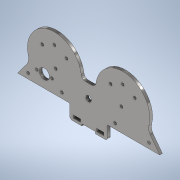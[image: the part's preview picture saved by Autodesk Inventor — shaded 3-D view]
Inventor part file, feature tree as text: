
AUTODESK INVENTOR PART (.ipt)
format: ipt  version: 2022 (Build 260153000, 153)  size: 521,216 bytes
history: native  units: mm
features: other x31, reference x18, sketch x7, chamfer x4, mirror x3, projected_geometry x3
ambient origin geometry x8: Origin, YZ Plane, XZ Plane, XY Plane, X Axis, Y Axis, Z Axis, Center Point
bodies: Body1 (feature_tree)
feature tree (66):
  other  "Твердое тело1"
  other  "Грань1"
  other  "Грань2"
  mirror  "Зеркальное отражение1"
  other  "УглСкругление1"
  other  "УглСкругление2"
  chamfer  "Фаска1"  Distance=1.0mm
  mirror  "Зеркальное отражение2"
  mirror  "Зеркальное отражение3"
  chamfer  "Фаска2"  Distance=3.0mm
  chamfer  "Фаска3"  Distance=3.0mm
  other  "Грань3"
  other  "УглСкругление3"
  chamfer  "Фаска4"  Distance=3.0mm
  sketch  "Эскиз1"
  reference  "Ссылка1"
  reference  "Ссылка2"
  other  "Пластина1"
  projected_geometry  "Спроецированная петля1"
  reference  "Ссылка3"
  other  "Пластина2"
  other  "Сгиб1"
  sketch  "Эскиз3"
  reference  "Ссылка4"
  reference  "Ссылка5"
  sketch  "Эскиз4"
  reference  "Ссылка6"
  sketch  "Эскиз6"
  reference  "Ссылка9"
  reference  "Ссылка10"
  sketch  "Эскиз8"
  reference  "Ссылка11"
  reference  "Ссылка12"
  reference  "Ссылка13"
  reference  "Ссылка14"
  sketch  "Эскиз10"
  reference  "Ссылка16"
  projected_geometry  "Спроецированная петля4"
  reference  "Ссылка17"
  reference  "Ссылка18"
  reference  "Ссылка19"
  other  "Пластина3"
  projected_geometry  "Спроецированная петля5"
  other  "Сгиб2"
  sketch  "Эскиз11"
  reference  "Ссылка20"
  reference  "Ссылка21"
  other  "Вырез1"
  other  "Вырез2"
  other  "Вырез3"
  other  "Вырез5"
  other  "Вырез7"
  other  "<userpath>\Documents\Git\MZCAT_2024\MZCAT.iam"
  other  "MZCAT.iam"
  other  "base:1"
  other  "motor:1"
  other  "CAT_wheel:1"
  other  "main_wheel_fixator:1"
  other  "<userpath>\Documents\Git\MZCAT_2024\MZCAT_4.iam"
  other  "MZCAT_4.iam"
  other  "lidar_krestovina_base:1"
  other  "motherCATboard:1"
  other  "CAT_protector:1"
  other  "<userpath>\Documents\Git\MZCAT_2024\MZCAT_3.iam"
  other  "MZCAT_3.iam"
  other  "motor:2"
